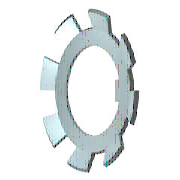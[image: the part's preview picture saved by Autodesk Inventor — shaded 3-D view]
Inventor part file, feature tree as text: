
AUTODESK INVENTOR PART (.ipt)
format: ipt  version: 2021 (Build 250183000, 183)  size: 231,424 bytes
history: native  units: mm (DEFAULTED — no unit token found)
features: sketch x2, extrude x2, pattern_circular x1, other x1, plane x1
ambient origin geometry x8: Origin, YZ Plane, XZ Plane, XY Plane, X Axis, Y Axis, Z Axis, Center Point
bodies: Solid1 (feature_tree), Body (feature_tree)
feature tree (7):
  sketch  "Sketch2"  dims[d3=148.0mm d4=170.0mm d5=4.363323mm d6=2.0mm d7=90.0deg d8=125.0mm d9=14.0mm d10=57.5mm d16=0.923998mm d17=2.0mm d18=0.0mm d19=2.0mm d20=0.0mm d21=170.0mm d23=360.0deg d24=0.0mm d25=0.0mm d26=90.0deg d27=0.0mm]
  extrude  "Cut"  Depth=2.0mm
  extrude  "Nib"  Depth=2.0mm
  pattern_circular  "Cuts"  [2 undecoded]
  other  "Work Axis1"
  plane  "Work Plane1"
  sketch  "Sketch1"  dims[d1=2.0mm d2=125.0mm]
note: 2 required parameter values undecoded (feature->parameter linkage not recoverable at this tier; creation-order binding heuristic only, values carry confidence <= 0.55)
